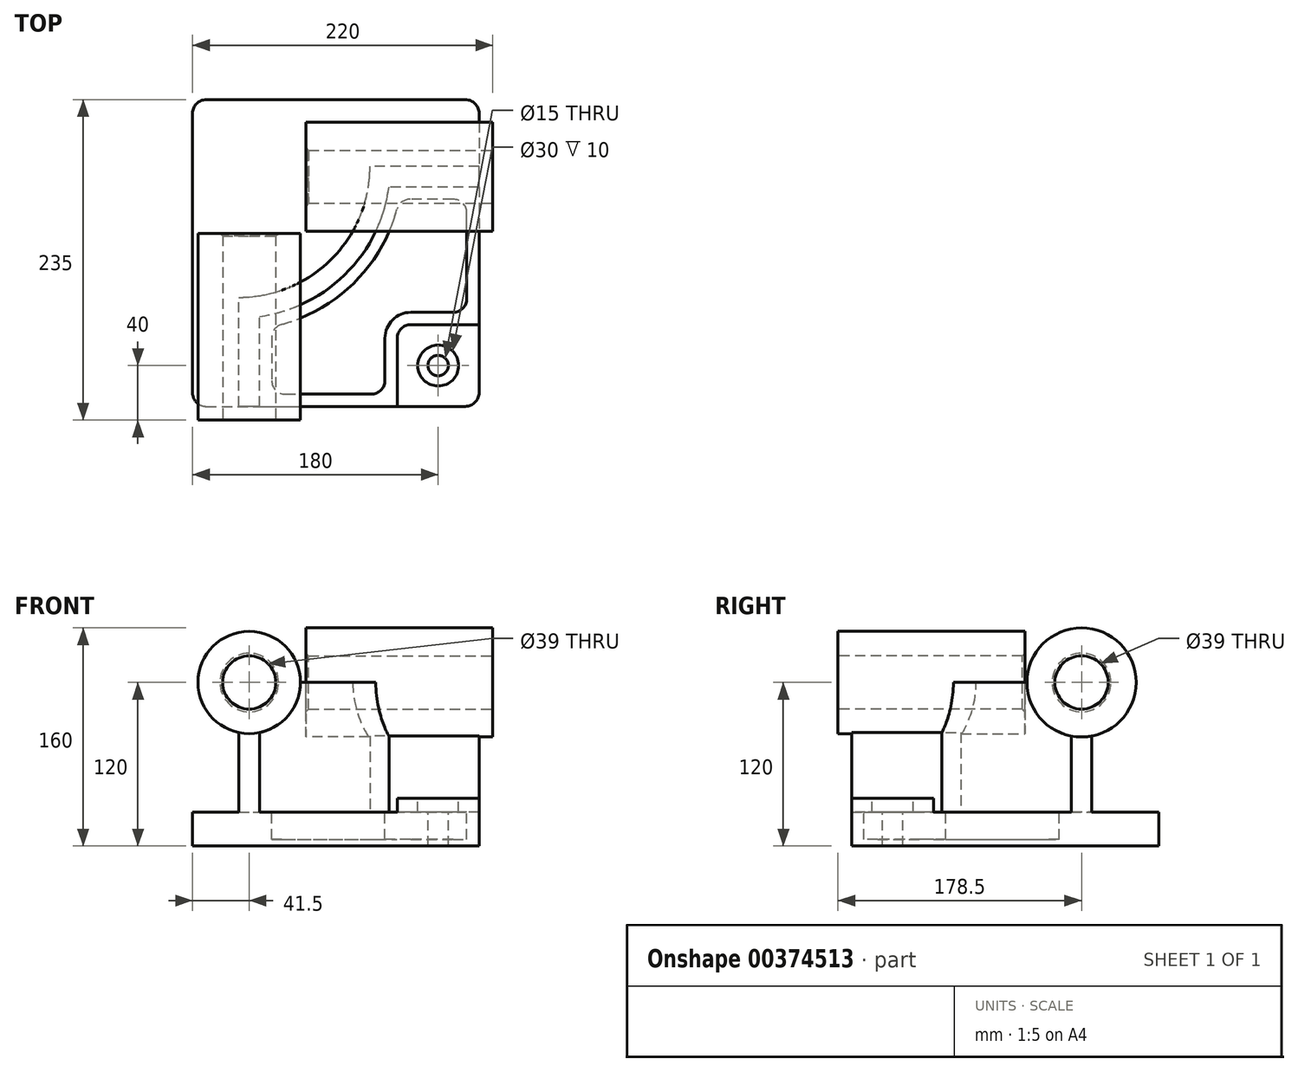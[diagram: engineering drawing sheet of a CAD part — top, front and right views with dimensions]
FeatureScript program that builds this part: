
annotation { "Feature Type Name" : "Feature", "Feature Type Description" : "" }
export const myFeature = defineFeature(function(context is Context, id is Id, definition is map)
    precondition{}
    {
        {
            var Q0;
            Q0=qCreatedBy(makeId("Top.planeOp"),FACE);
            var sketch = newSketch(context, id + "F0", { "sketchPlane" : qUnion([Q0])});
            skLineSegment(sketch, "E0.bottom", {"start": v(-105, 112.5) * mm, "end": v(105, 112.5) * mm});
            skLineSegment(sketch, "E0.top", {"start": v(-105, -112.5) * mm, "end": v(105, -112.5) * mm});
            skLineSegment(sketch, "E0.left", {"start": v(-105, 112.5) * mm, "end": v(-105, -112.5) * mm});
            skLineSegment(sketch, "E0.right", {"start": v(105, 112.5) * mm, "end": v(105, -112.5) * mm});
            skPoint(sketch, "E0.middle", {"position": v(0, 0) * mm});
            skSolve(sketch);
        }
        {
            var Q0;
            Q0=makeQuery(id+"F0.imprint","IMPRINT",FACE,{"disambiguationData":[TD([[makeQuery(id+"F0.imprint","IMPRINT",EDGE,{"derivedFrom":sQuery(id+"F0.wireOp",EDGE,"E0.bottom")}),-1.0]])]});
            extrude(context, id + "F1", {"entities" : qUnion([Q0]), "depth" : 25 * mm});
        }
        {
            var Q0;
            Q0=makeQuery(id+"F1.opExtrude","CAP_FACE",FACE,{"disambiguationData":[OSD([sQuery(id+"F0.wireOp",EDGE,"E0.bottom"),sQuery(id+"F0.wireOp",EDGE,"E0.top"),sQuery(id+"F0.wireOp",EDGE,"E0.left"),sQuery(id+"F0.wireOp",EDGE,"E0.right")])],"isStart":false});
            var sketch = newSketch(context, id + "F2", { "sketchPlane" : qUnion([Q0])});
            skLineSegment(sketch, "E1", {"start": v(-71, -112.5) * mm, "end": v(-71, -32.5) * mm});
            skLineSegment(sketch, "E2", {"start": v(105, 63.5) * mm, "end": v(25, 63.5) * mm});
            skArc(sketch, "E3", {"start": v(-71, -32.5) * mm, "mid": v(-3.12, -4.38) * mm, "end": v(25, 63.5) * mm});
            skLineSegment(sketch, "E4", {"start": v(-71, 63.5) * mm, "end": v(25, 63.5) * mm, "construction": true});
            skLineSegment(sketch, "E5", {"start": v(-71, 63.5) * mm, "end": v(-71, -32.5) * mm, "construction": true});
            skLineSegment(sketch, "E6.0", {"start": v(105, 48.5) * mm, "end": v(38.98, 48.5) * mm});
            skArc(sketch, "E6.1", {"start": v(-56, -46.48) * mm, "mid": v(7.49, -14.99) * mm, "end": v(38.98, 48.5) * mm});
            skLineSegment(sketch, "E6.2", {"start": v(-56, -112.5) * mm, "end": v(-56, -46.48) * mm});
            skLineSegment(sketch, "E7.0", {"start": v(-105, -112.5) * mm, "end": v(105, -112.5) * mm});
            skLineSegment(sketch, "E8.0", {"start": v(105, 112.5) * mm, "end": v(105, -112.5) * mm});
            skSolve(sketch);
        }
        {
            var Q0;
            {var subQ2=sQuery(id+"F2.wireOp",EDGE,"E1");Q0=makeQuery(id+"F2.imprint","IMPRINT",FACE,{"disambiguationData":[TD([[makeQuery(id+"F2.imprint","IMPRINT",EDGE,{"derivedFrom":subQ2}),-1.0]])]});}
            extrude(context, id + "F3", {"entities" : qUnion([Q0]), "operationType" : NewBodyOperationType.ADD, "depth" : 95 * mm});
        }
        {
            var Q0;
            Q0=makeQuery(id+"F3.boolean.opBoolean","MERGE",FACE,{"derivedFrom":[makeQuery(id+"F1.opExtrude","SWEPT_FACE",FACE,{"disambiguationData":[OSD([sQuery(id+"F0.wireOp",EDGE,"E0.top")])]}),makeQuery(id+"F3.opExtrude","SWEPT_FACE",FACE,{"disambiguationData":[OSD([sQuery(id+"F2.wireOp",EDGE,"E7.0")])]})]});
            var sketch = newSketch(context, id + "F4", { "sketchPlane" : qUnion([Q0])});
            skCircle(sketch, "E9", {"center": v(-63.5, 120) * mm, "radius": 37.5 * mm});
            skSolve(sketch);
        }
        {
            var Q0;
            Q0 = qSketchRegion(id + "F4", true);
            extrude(context, id + "F5", {"entities" : qUnion([Q0]), "operationType" : NewBodyOperationType.ADD, "depth" : 10 * mm, "hasSecondDirection" : true, "secondDirectionOppositeDirection" : true, "secondDirectionDepth" : (137 - 10) * mm});
        }
        {
            var Q0;
            Q0=makeQuery(id+"F3.boolean.opBoolean","MERGE",FACE,{"derivedFrom":[makeQuery(id+"F1.opExtrude","SWEPT_FACE",FACE,{"disambiguationData":[OSD([sQuery(id+"F0.wireOp",EDGE,"E0.right")])]}),makeQuery(id+"F3.opExtrude","SWEPT_FACE",FACE,{"disambiguationData":[OSD([sQuery(id+"F2.wireOp",EDGE,"E8.0")])]})]});
            var sketch = newSketch(context, id + "F6", { "sketchPlane" : qUnion([Q0])});
            skCircle(sketch, "E10", {"center": v(56, 120) * mm, "radius": 40 * mm});
            skSolve(sketch);
        }
        {
            var Q0;
            Q0 = qSketchRegion(id + "F6", true);
            extrude(context, id + "F7", {"entities" : qUnion([Q0]), "operationType" : NewBodyOperationType.ADD, "depth" : 10 * mm, "hasSecondDirection" : true, "secondDirectionOppositeDirection" : true, "secondDirectionDepth" : (137 - 10) * mm});
        }
        {
            var Q0;
            {var subQ0=sQuery(id+"F0.wireOp",EDGE,"E0.right");var subQ1=sQuery(id+"F0.wireOp",EDGE,"E0.top");Q0=makeQuery(id+"F3.boolean.opBoolean","SPLIT",FACE,{"disambiguationData":[TD([makeQuery(id+"F3.opExtrude","SWEPT_FACE",FACE,{"disambiguationData":[OSD([sQuery(id+"F2.wireOp",EDGE,"E6.0")])]})])],"derivedFrom":makeQuery(id+"F1.opExtrude","CAP_FACE",FACE,{"disambiguationData":[OSD([sQuery(id+"F0.wireOp",EDGE,"E0.bottom"),subQ1,sQuery(id+"F0.wireOp",EDGE,"E0.left"),subQ0])],"isStart":false})});}
            var sketch = newSketch(context, id + "F8", { "sketchPlane" : qUnion([Q0])});
            skLineSegment(sketch, "E11.bottom", {"start": v(105, -112.5) * mm, "end": v(45, -112.5) * mm});
            skLineSegment(sketch, "E11.top", {"start": v(105, -52.5) * mm, "end": v(45, -52.5) * mm});
            skLineSegment(sketch, "E11.left", {"start": v(105, -112.5) * mm, "end": v(105, -52.5) * mm});
            skLineSegment(sketch, "E11.right", {"start": v(45, -112.5) * mm, "end": v(45, -52.5) * mm});
            skSolve(sketch);
        }
        {
            var Q0;
            Q0 = qSketchRegion(id + "F8", true);
            extrude(context, id + "F9", {"entities" : qUnion([Q0]), "operationType" : NewBodyOperationType.ADD, "depth" : 10 * mm});
        }
        {
            var Q0;
            Q0=makeQuery(id+"F9.opExtrude","SWEPT_EDGE",EDGE,{"disambiguationData":[OSD([sQuery(id+"F8.wireOp",EDGE,"E11.top"),sQuery(id+"F8.wireOp",EDGE,"E11.right")])]});
            fillet(context, id + "F10", {"entities" : qUnion([Q0]), "radius" : 10 * mm, "tangentPropagation" : true, "allowEdgeOverflow" : false});
        }
        {
            var Q0;
            {var subQ0=sQuery(id+"F0.wireOp",EDGE,"E0.right");var subQ1=sQuery(id+"F0.wireOp",EDGE,"E0.top");Q0=makeQuery(id+"F3.boolean.opBoolean","SPLIT",FACE,{"disambiguationData":[TD([makeQuery(id+"F3.opExtrude","SWEPT_FACE",FACE,{"disambiguationData":[OSD([sQuery(id+"F2.wireOp",EDGE,"E6.0")])]})])],"derivedFrom":makeQuery(id+"F1.opExtrude","CAP_FACE",FACE,{"disambiguationData":[OSD([sQuery(id+"F0.wireOp",EDGE,"E0.bottom"),subQ1,sQuery(id+"F0.wireOp",EDGE,"E0.left"),subQ0])],"isStart":false})});}
            var sketch = newSketch(context, id + "F11", { "sketchPlane" : qUnion([Q0])});
            skLineSegment(sketch, "E12.0", {"start": v(-47, -54.08) * mm, "end": v(-47, -103.5) * mm});
            skArc(sketch, "E12.1", {"start": v(46.58, 39.5) * mm, "mid": v(13.85, -21.35) * mm, "end": v(-47, -54.08) * mm});
            skLineSegment(sketch, "E12.2", {"start": v(-47, -103.5) * mm, "end": v(36, -103.5) * mm});
            skLineSegment(sketch, "E12.3", {"start": v(96, 39.5) * mm, "end": v(46.58, 39.5) * mm});
            skLineSegment(sketch, "E12.4", {"start": v(36, -103.5) * mm, "end": v(36, -62.5) * mm});
            skArc(sketch, "E12.5", {"start": v(36, -62.5) * mm, "mid": v(41.56, -49.06) * mm, "end": v(55, -43.5) * mm});
            skLineSegment(sketch, "E12.6", {"start": v(55, -43.5) * mm, "end": v(96, -43.5) * mm});
            skLineSegment(sketch, "E12.7", {"start": v(96, -43.5) * mm, "end": v(96, 39.5) * mm});
            skSolve(sketch);
        }
        {
            var Q0;
            Q0=makeQuery(id+"F11.imprint","IMPRINT",FACE,{"disambiguationData":[TD([[makeQuery(id+"F11.imprint","IMPRINT",EDGE,{"derivedFrom":sQuery(id+"F11.wireOp",EDGE,"E12.0")}),1.0]])]});
            extrude(context, id + "F12", {"entities" : qUnion([Q0]), "operationType" : NewBodyOperationType.REMOVE, "oppositeDirection" : true, "depth" : 20 * mm});
        }
        {
            var Q0;
            Q0=makeQuery(id+"F9.opExtrude","CAP_FACE",FACE,{"disambiguationData":[OSD([sQuery(id+"F8.wireOp",EDGE,"E11.bottom"),sQuery(id+"F8.wireOp",EDGE,"E11.top"),sQuery(id+"F8.wireOp",EDGE,"E11.left"),sQuery(id+"F8.wireOp",EDGE,"E11.right")])],"isStart":false});
            var sketch = newSketch(context, id + "F13", { "sketchPlane" : qUnion([Q0])});
            skCircle(sketch, "E13", {"center": v(75, -82.5) * mm, "radius": 15 * mm});
            skSolve(sketch);
        }
        {
            var Q0;
            Q0=sQuery(id+"F13.wireOp",VERTEX,"E13.center");
            var Q1;
            Q1=makeQuery(id+"F1.opExtrude","SWEPT_BODY",BODY,{"disambiguationData":[OSD([sQuery(id+"F0.wireOp",EDGE,"E0.bottom"),sQuery(id+"F0.wireOp",EDGE,"E0.top"),sQuery(id+"F0.wireOp",EDGE,"E0.left"),sQuery(id+"F0.wireOp",EDGE,"E0.right")])]});
            hole(context, id + "F14", {"style" : HoleStyle.C_BORE, "endStyle" : HoleEndStyle.THROUGH, "holeDiameter" : 15 * mm, "cBoreDiameter" : 30 * mm, "cBoreDepth" : 10 * mm, "isTappedThrough" : true, "tappedDepth" : 12 * mm, "tapClearance" : 3, "locations" : qUnion([Q0]), "scope" : qUnion([Q1])});
        }
        {
            var Q0;
            Q0=makeQuery(id+"F12.boolean.opBoolean","COPY",EDGE,{"derivedFrom":makeQuery(id+"F12.opExtrude","SWEPT_EDGE",EDGE,{"disambiguationData":[OSD([sQuery(id+"F11.wireOp",EDGE,"E12.1"),sQuery(id+"F11.wireOp",EDGE,"E12.3")])]})});
            var Q1;
            Q1=makeQuery(id+"F12.boolean.opBoolean","COPY",EDGE,{"derivedFrom":makeQuery(id+"F12.opExtrude","SWEPT_EDGE",EDGE,{"disambiguationData":[OSD([sQuery(id+"F11.wireOp",EDGE,"E12.0"),sQuery(id+"F11.wireOp",EDGE,"E12.1")])]})});
            var Q2;
            Q2=makeQuery(id+"F12.boolean.opBoolean","COPY",EDGE,{"derivedFrom":makeQuery(id+"F12.opExtrude","SWEPT_EDGE",EDGE,{"disambiguationData":[OSD([sQuery(id+"F11.wireOp",EDGE,"E12.0"),sQuery(id+"F11.wireOp",EDGE,"E12.2")])]})});
            var Q3;
            Q3=makeQuery(id+"F12.boolean.opBoolean","COPY",EDGE,{"derivedFrom":makeQuery(id+"F12.opExtrude","SWEPT_EDGE",EDGE,{"disambiguationData":[OSD([sQuery(id+"F11.wireOp",EDGE,"E12.3"),sQuery(id+"F11.wireOp",EDGE,"E12.7")])]})});
            var Q4;
            Q4=makeQuery(id+"F12.boolean.opBoolean","COPY",EDGE,{"derivedFrom":makeQuery(id+"F12.opExtrude","SWEPT_EDGE",EDGE,{"disambiguationData":[OSD([sQuery(id+"F11.wireOp",EDGE,"E12.2"),sQuery(id+"F11.wireOp",EDGE,"E12.4")])]})});
            var Q5;
            Q5=makeQuery(id+"F12.boolean.opBoolean","COPY",EDGE,{"derivedFrom":makeQuery(id+"F12.opExtrude","SWEPT_EDGE",EDGE,{"disambiguationData":[OSD([sQuery(id+"F11.wireOp",EDGE,"E12.6"),sQuery(id+"F11.wireOp",EDGE,"E12.7")])]})});
            fillet(context, id + "F15", {"entities" : qUnion([Q0, Q1, Q2, Q3, Q4, Q5]), "radius" : 10 * mm, "tangentPropagation" : true, "allowEdgeOverflow" : false});
        }
        {
            var Q0;
            Q0=makeQuery(id+"F5.opExtrude","CAP_FACE",FACE,{"disambiguationData":[OSD([sQuery(id+"F4.wireOp",EDGE,"E9")])],"isStart":false});
            var sketch = newSketch(context, id + "F16", { "sketchPlane" : qUnion([Q0])});
            skCircle(sketch, "E14", {"center": v(-63.5, 120) * mm, "radius": 19.5 * mm});
            skSolve(sketch);
        }
        {
            var Q0;
            Q0 = qSketchRegion(id + "F16", true);
            extrude(context, id + "F17", {"entities" : qUnion([Q0]), "operationType" : NewBodyOperationType.REMOVE, "endBound" : BoundingType.THROUGH_ALL, "oppositeDirection" : true, "depth" : 25 * mm});
        }
        {
            var Q0;
            Q0=makeQuery(id+"F7.opExtrude","CAP_FACE",FACE,{"disambiguationData":[OSD([sQuery(id+"F6.wireOp",EDGE,"E10")])],"isStart":false});
            var sketch = newSketch(context, id + "F18", { "sketchPlane" : qUnion([Q0])});
            skCircle(sketch, "E15", {"center": v(56, 120) * mm, "radius": 19.5 * mm});
            skSolve(sketch);
        }
        {
            var Q0;
            Q0 = qSketchRegion(id + "F18", true);
            extrude(context, id + "F19", {"entities" : qUnion([Q0]), "operationType" : NewBodyOperationType.REMOVE, "endBound" : BoundingType.THROUGH_ALL, "oppositeDirection" : true, "depth" : 25 * mm});
        }
        {
            var Q0;
            Q0=makeQuery(id+"F17.boolean.opBoolean","COPY",EDGE,{"derivedFrom":makeQuery(id+"F17.opExtrude","CAP_EDGE",EDGE,{"disambiguationData":[OSD([sQuery(id+"F16.wireOp",EDGE,"E14")])],"isStart":true})});
            var Q1;
            Q1=makeQuery(id+"F19.boolean.opBoolean","COPY",EDGE,{"derivedFrom":makeQuery(id+"F19.opExtrude","CAP_EDGE",EDGE,{"disambiguationData":[OSD([sQuery(id+"F18.wireOp",EDGE,"E15")])],"isStart":true})});
            var Q2;
            Q2=makeQuery(id+"F17.boolean.opBoolean","INTERSECT",EDGE,{"derivedFrom":[makeQuery(id+"F5.opExtrude","CAP_FACE",FACE,{"disambiguationData":[OSD([sQuery(id+"F4.wireOp",EDGE,"E9")])],"isStart":true}),makeQuery(id+"F17.opExtrude","SWEPT_FACE",FACE,{"disambiguationData":[OSD([sQuery(id+"F16.wireOp",EDGE,"E14")])]})]});
            var Q3;
            Q3=makeQuery(id+"F19.boolean.opBoolean","INTERSECT",EDGE,{"derivedFrom":[makeQuery(id+"F7.opExtrude","CAP_FACE",FACE,{"disambiguationData":[OSD([sQuery(id+"F6.wireOp",EDGE,"E10")])],"isStart":true}),makeQuery(id+"F19.opExtrude","SWEPT_FACE",FACE,{"disambiguationData":[OSD([sQuery(id+"F18.wireOp",EDGE,"E15")])]})]});
            chamfer(context, id + "F20", {"entities" : qUnion([Q0, Q1, Q2, Q3]), "width" : 2 * mm, "tangentPropagation" : true});
        }
        {
            var Q0;
            Q0=makeQuery(id+"F9.boolean.opBoolean","MERGE",EDGE,{"derivedFrom":[makeQuery(id+"F1.opExtrude","SWEPT_EDGE",EDGE,{"disambiguationData":[OSD([sQuery(id+"F0.wireOp",EDGE,"E0.top"),sQuery(id+"F0.wireOp",EDGE,"E0.right")])]}),makeQuery(id+"F9.opExtrude","SWEPT_EDGE",EDGE,{"disambiguationData":[OSD([sQuery(id+"F8.wireOp",EDGE,"E11.bottom"),sQuery(id+"F8.wireOp",EDGE,"E11.left")])]})]});
            var Q1;
            Q1=makeQuery(id+"F1.opExtrude","SWEPT_EDGE",EDGE,{"disambiguationData":[OSD([sQuery(id+"F0.wireOp",EDGE,"E0.bottom"),sQuery(id+"F0.wireOp",EDGE,"E0.right")])]});
            var Q2;
            Q2=makeQuery(id+"F1.opExtrude","SWEPT_EDGE",EDGE,{"disambiguationData":[OSD([sQuery(id+"F0.wireOp",EDGE,"E0.bottom"),sQuery(id+"F0.wireOp",EDGE,"E0.left")])]});
            var Q3;
            Q3=makeQuery(id+"F1.opExtrude","SWEPT_EDGE",EDGE,{"disambiguationData":[OSD([sQuery(id+"F0.wireOp",EDGE,"E0.top"),sQuery(id+"F0.wireOp",EDGE,"E0.left")])]});
            fillet(context, id + "F21", {"entities" : qUnion([Q0, Q1, Q2, Q3]), "radius" : 10 * mm, "tangentPropagation" : true, "allowEdgeOverflow" : false});
        }
    });
